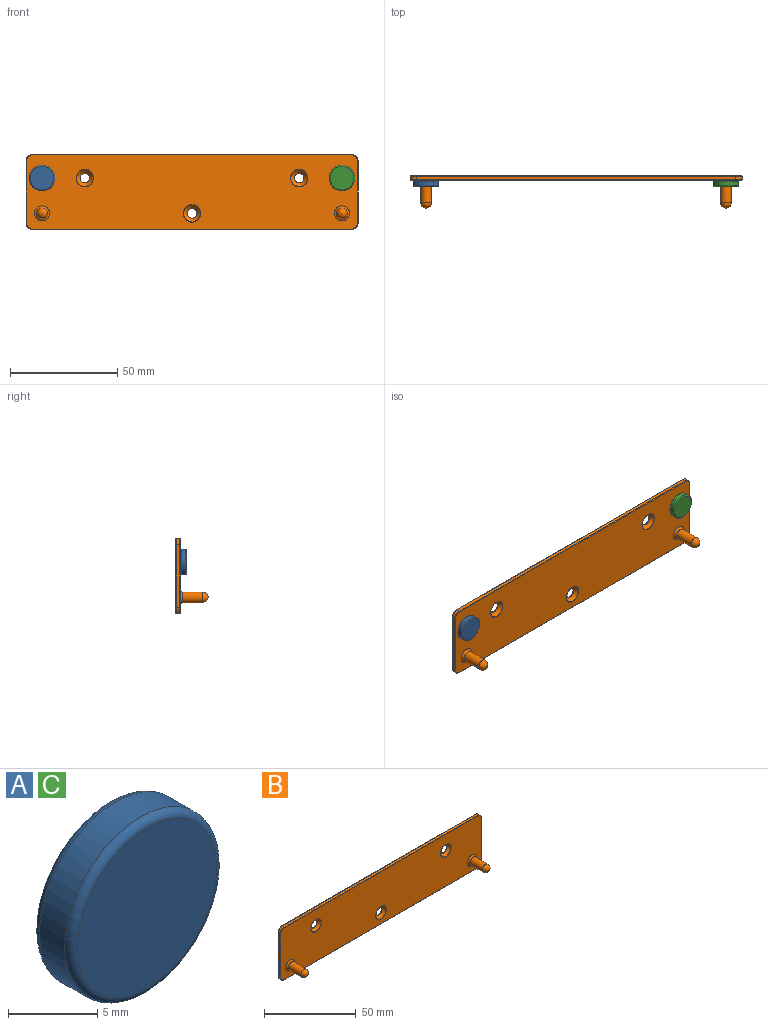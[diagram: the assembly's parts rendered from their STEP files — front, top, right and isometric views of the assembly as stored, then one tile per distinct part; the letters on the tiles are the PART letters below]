
ASSEMBLY  parts=3 mates=2
PART A: 5 faces, bbox 13x3x13 mm
  f0: cylinder r=6mm len=12mm, axis (0,-1,0), area 75.4mm2, adj f3,f4
  f1: plane 11x11mm, normal (0,1,0), area 95mm2, adj f4
  f2: plane 11x11mm, normal (0,-1,0), area 95mm2, adj f3
  f3: torus R=5.5mm, axis (0,1,0), area 28.7mm2, adj f0,f2
  f4: torus R=5.5mm, axis (0,1,0), area 28.7mm2, adj f0,f1
PART B: 41 faces, bbox 155.5x15x35.5 mm
  f0: plane 149x1.6mm, normal (0,0,1), area 238.4mm2, adj f1,f7,f32,f40
  f1: cylinder r=3mm len=3mm, axis (0,1,0), area 7.5mm2, adj f0,f2,f30,f38
  f2: plane 29x1.6mm, normal (1,0,0), area 46.4mm2, adj f1,f3,f28,f36
  f3: cylinder r=3mm len=3mm, axis (0,1,0), area 7.5mm2, adj f2,f4,f26,f34
  f4: plane 149x1.6mm, normal (0,0,-1), area 238.4mm2, adj f3,f5,f25,f33
  f5: cylinder r=3mm len=3mm, axis (0,1,0), area 7.5mm2, adj f4,f6,f27,f35
  f6: plane 29x1.6mm, normal (-1,0,0), area 46.4mm2, adj f5,f7,f29,f37
  f7: cylinder r=3mm len=3mm, axis (0,1,0), area 7.5mm2, adj f0,f6,f31,f39
  f8: plane 154.6x34.6mm, normal (0,-1,0), area 5108.4mm2, adj f15,f16,f19,f20,f21,f33,f34,f35
  f9: plane 154.6x34.6mm, normal (0,1,0), area 5284.3mm2, adj f22,f23,f24,f25,f26,f27,f28,f29
  f10: cylinder r=2.5mm len=9.5mm, axis (0,1,0), area 149.2mm2, adj f16,f18
  f11: cylinder r=2.5mm len=9.5mm, axis (0,1,0), area 149.2mm2, adj f15,f17
  f12: cone r=4mm half-angle=45deg, axis (0,-1,0), area 44.7mm2, adj f19,f23
  f13: cone r=4mm half-angle=45deg, axis (0,-1,0), area 44.7mm2, adj f20,f24
  f14: cone r=2mm half-angle=45deg, axis (0,-1,0), area 44.7mm2, adj f21,f22
  f15: torus R=3.5mm, axis (0,1,0), area 28.3mm2, adj f8,f11
  f16: torus R=3.5mm, axis (0,1,0), area 28.3mm2, adj f8,f10
  f17: sphere r=2.5mm, area 39.3mm2, adj f11
  f18: sphere r=2.5mm, area 39.3mm2, adj f10
  f19: torus R=4.08mm, axis (0,1,0), area 4mm2, adj f8,f12
  f20: torus R=4.08mm, axis (0,1,0), area 4mm2, adj f8,f13
  f21: torus R=4.08mm, axis (0,1,0), area 4mm2, adj f8,f14
  f22: torus R=2.48mm, axis (0,1,0), area 6.9mm2, adj f9,f14
  f23: torus R=2.48mm, axis (0,1,0), area 6.9mm2, adj f9,f12
  f24: torus R=2.48mm, axis (0,1,0), area 6.9mm2, adj f9,f13
  f25: cylinder r=0.2mm len=149mm, axis (-1,0,0), area 46.8mm2, adj f4,f9,f26,f27
  f26: torus R=2.8mm, axis (0,1,0), area 1.4mm2, adj f3,f9,f25,f28
  f27: torus R=2.8mm, axis (0,1,0), area 1.4mm2, adj f5,f9,f25,f29
  f28: cylinder r=0.2mm len=29mm, axis (0,0,-1), area 9.1mm2, adj f2,f9,f26,f30
  f29: cylinder r=0.2mm len=29mm, axis (0,0,1), area 9.1mm2, adj f6,f9,f27,f31
  f30: torus R=2.8mm, axis (0,1,0), area 1.4mm2, adj f1,f9,f28,f32
  f31: torus R=2.8mm, axis (0,1,0), area 1.4mm2, adj f7,f9,f29,f32
  f32: cylinder r=0.2mm len=149mm, axis (1,0,0), area 46.8mm2, adj f0,f9,f30,f31
  f33: cylinder r=0.2mm len=149mm, axis (1,0,0), area 46.8mm2, adj f4,f8,f34,f35
  f34: torus R=2.8mm, axis (0,1,0), area 1.4mm2, adj f3,f8,f33,f36
  f35: torus R=2.8mm, axis (0,1,0), area 1.4mm2, adj f5,f8,f33,f37
  f36: cylinder r=0.2mm len=29mm, axis (0,0,1), area 9.1mm2, adj f2,f8,f34,f38
  f37: cylinder r=0.2mm len=29mm, axis (0,0,-1), area 9.1mm2, adj f6,f8,f35,f39
  f38: torus R=2.8mm, axis (0,1,0), area 1.4mm2, adj f1,f8,f36,f40
  f39: torus R=2.8mm, axis (0,1,0), area 1.4mm2, adj f7,f8,f37,f40
  f40: cylinder r=0.2mm len=149mm, axis (-1,0,0), area 46.8mm2, adj f0,f8,f38,f39
PART C: same geometry as A
PLACE A t=(-145.5,-7,9)mm
PLACE B t=(-5.5,-2,9)mm
PLACE C t=(-5.5,-7,9)mm
MATE fastened A.f0 <-> B.f8  axis (0,1,0) through (-75.5,16,9)mm
MATE fastened C.f0 <-> B.f8  axis (0,1,0) through (64.5,16,9)mm
